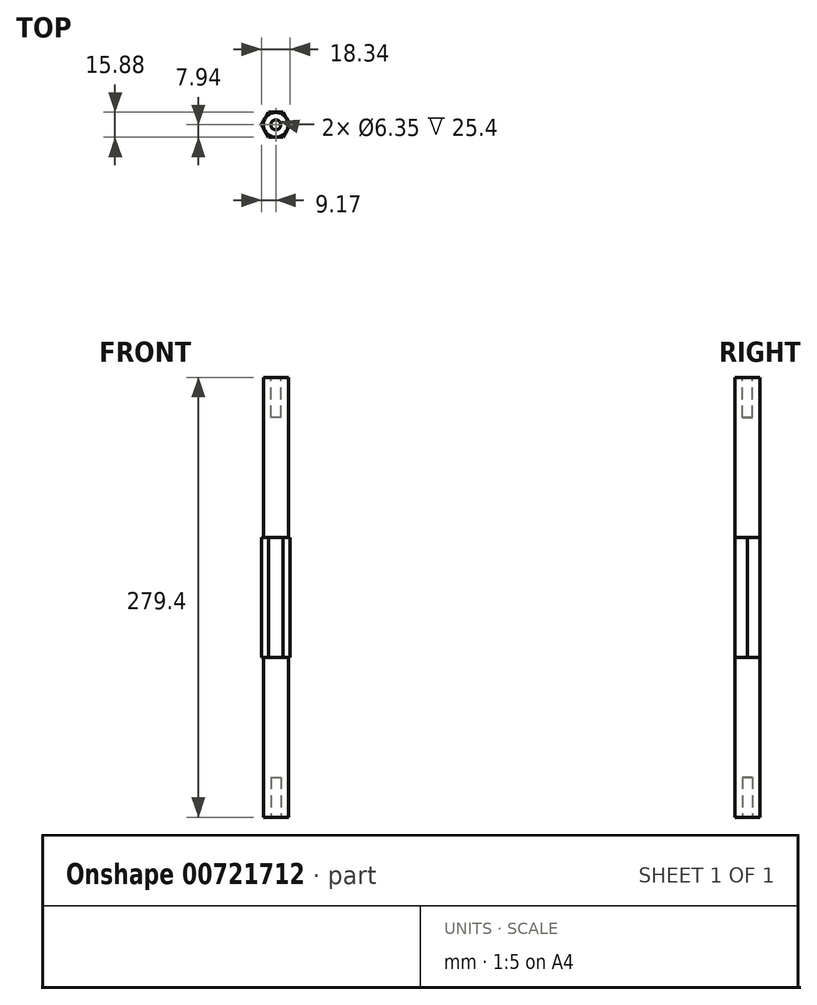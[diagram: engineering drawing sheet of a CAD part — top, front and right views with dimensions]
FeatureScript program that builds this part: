
annotation { "Feature Type Name" : "Feature", "Feature Type Description" : "" }
export const myFeature = defineFeature(function(context is Context, id is Id, definition is map)
    precondition{}
    {
        {
            var Q0;
            Q0=qCreatedBy(makeId("Top.planeOp"),FACE);
            var sketch = newSketch(context, id + "F0", { "sketchPlane" : qUnion([Q0])});
            skCircle(sketch, "E0", {"center": v(0, 0) * mm, "radius": 7.94 * mm, "construction": true});
            skLineSegment(sketch, "E1", {"start": v(-56.7, 0) * mm, "end": v(63.32, 0) * mm, "construction": true});
            skLineSegment(sketch, "E2", {"start": v(0, -40.46) * mm, "end": v(0, 43.76) * mm, "construction": true});
            skLineSegment(sketch, "E3", {"start": v(0, 0) * mm, "end": v(-27.5, -15.88) * mm, "construction": true});
            skLineSegment(sketch, "E4", {"start": v(0, 0) * mm, "end": v(28.61, -16.52) * mm, "construction": true});
            skLineSegment(sketch, "E5.MirrorCS", {"start": v(0, 0) * mm, "end": v(28.61, 16.52) * mm, "construction": true});
            skLineSegment(sketch, "E6.MirrorCS", {"start": v(0, 0) * mm, "end": v(-27.5, 15.88) * mm, "construction": true});
            skLineSegment(sketch, "E7", {"start": v(-9.17, 0) * mm, "end": v(-4.58, -7.94) * mm});
            skLineSegment(sketch, "E8", {"start": v(-9.17, 0) * mm, "end": v(-4.58, 7.94) * mm});
            skLineSegment(sketch, "E9.trimOffspring", {"start": v(-4.58, -7.94) * mm, "end": v(26.02, -7.94) * mm});
            skLineSegment(sketch, "E10.trimOffspring", {"start": v(-4.58, 7.94) * mm, "end": v(4.58, 7.94) * mm});
            skLineSegment(sketch, "E11.MirrorCS", {"start": v(9.17, 0) * mm, "end": v(4.58, -7.94) * mm});
            skLineSegment(sketch, "E12.MirrorCS", {"start": v(9.17, 0) * mm, "end": v(4.58, 7.94) * mm});
            skSolve(sketch);
        }
        {
            var Q0;
            Q0=qSketchRegion(id+"F0",true);
            extrude(context, id + "F1", {"entities" : qUnion([Q0]), "depth" : 279.4 * mm, "offsetDistance" : 25.4 * mm});
        }
        {
            var Q0;
            Q0=makeQuery(id+"F1.opExtrude","CAP_FACE",FACE,{"disambiguationData":[OSD([sQuery(id+"F0.wireOp",EDGE,"E7"),sQuery(id+"F0.wireOp",EDGE,"E8"),sQuery(id+"F0.wireOp",EDGE,"E9.trimOffspring"),sQuery(id+"F0.wireOp",EDGE,"E10.trimOffspring"),sQuery(id+"F0.wireOp",EDGE,"E11.MirrorCS"),sQuery(id+"F0.wireOp",EDGE,"E12.MirrorCS")])],"isStart":true});
            var sketch = newSketch(context, id + "F2", { "sketchPlane" : qUnion([Q0])});
            skCircle(sketch, "E13", {"center": v(0, 0) * mm, "radius": 7.94 * mm});
            skCircle(sketch, "E14", {"center": v(0, 0) * mm, "radius": 9.17 * mm});
            skSolve(sketch);
        }
        {
            var Q0;
            Q0=qSketchRegion(id+"F2",true);
            extrude(context, id + "F3", {"entities" : qUnion([Q0]), "operationType" : NewBodyOperationType.REMOVE, "oppositeDirection" : true, "depth" : 101.6 * mm, "offsetDistance" : 25.4 * mm});
        }
        {
            var Q0;
            Q0=makeQuery(id+"F1.opExtrude","CAP_FACE",FACE,{"disambiguationData":[OSD([sQuery(id+"F0.wireOp",EDGE,"E7"),sQuery(id+"F0.wireOp",EDGE,"E8"),sQuery(id+"F0.wireOp",EDGE,"E9.trimOffspring"),sQuery(id+"F0.wireOp",EDGE,"E10.trimOffspring"),sQuery(id+"F0.wireOp",EDGE,"E11.MirrorCS"),sQuery(id+"F0.wireOp",EDGE,"E12.MirrorCS")])],"isStart":false});
            var sketch = newSketch(context, id + "F4", { "sketchPlane" : qUnion([Q0])});
            skCircle(sketch, "E15", {"center": v(0, 0) * mm, "radius": 7.94 * mm});
            skCircle(sketch, "E16", {"center": v(0, 0) * mm, "radius": 9.17 * mm});
            skSolve(sketch);
        }
        {
            var Q0;
            Q0=qSketchRegion(id+"F4",true);
            extrude(context, id + "F5", {"entities" : qUnion([Q0]), "operationType" : NewBodyOperationType.REMOVE, "oppositeDirection" : true, "depth" : 101.6 * mm, "offsetDistance" : 25.4 * mm});
        }
        {
            var Q0;
            Q0=makeQuery(id+"F1.opExtrude","CAP_FACE",FACE,{"disambiguationData":[OSD([sQuery(id+"F0.wireOp",EDGE,"E7"),sQuery(id+"F0.wireOp",EDGE,"E8"),sQuery(id+"F0.wireOp",EDGE,"E9.trimOffspring"),sQuery(id+"F0.wireOp",EDGE,"E10.trimOffspring"),sQuery(id+"F0.wireOp",EDGE,"E11.MirrorCS"),sQuery(id+"F0.wireOp",EDGE,"E12.MirrorCS")])],"isStart":true});
            var sketch = newSketch(context, id + "F6", { "sketchPlane" : qUnion([Q0])});
            skCircle(sketch, "E17", {"center": v(0, 0) * mm, "radius": 3.18 * mm});
            skSolve(sketch);
        }
        {
            var Q0;
            Q0=qSketchRegion(id+"F6",true);
            extrude(context, id + "F7", {"entities" : qUnion([Q0]), "operationType" : NewBodyOperationType.REMOVE, "oppositeDirection" : true, "depth" : 25.4 * mm, "offsetDistance" : 25.4 * mm});
        }
        {
            var Q0;
            Q0=makeQuery(id+"F1.opExtrude","CAP_FACE",FACE,{"disambiguationData":[OSD([sQuery(id+"F0.wireOp",EDGE,"E7"),sQuery(id+"F0.wireOp",EDGE,"E8"),sQuery(id+"F0.wireOp",EDGE,"E9.trimOffspring"),sQuery(id+"F0.wireOp",EDGE,"E10.trimOffspring"),sQuery(id+"F0.wireOp",EDGE,"E11.MirrorCS"),sQuery(id+"F0.wireOp",EDGE,"E12.MirrorCS")])],"isStart":false});
            var sketch = newSketch(context, id + "F8", { "sketchPlane" : qUnion([Q0])});
            skCircle(sketch, "E18", {"center": v(0, 0) * mm, "radius": 3.18 * mm});
            skSolve(sketch);
        }
        {
            var Q0;
            Q0=qSketchRegion(id+"F8",true);
            extrude(context, id + "F9", {"entities" : qUnion([Q0]), "operationType" : NewBodyOperationType.REMOVE, "oppositeDirection" : true, "depth" : 25.4 * mm, "offsetDistance" : 25.4 * mm});
        }
    });
